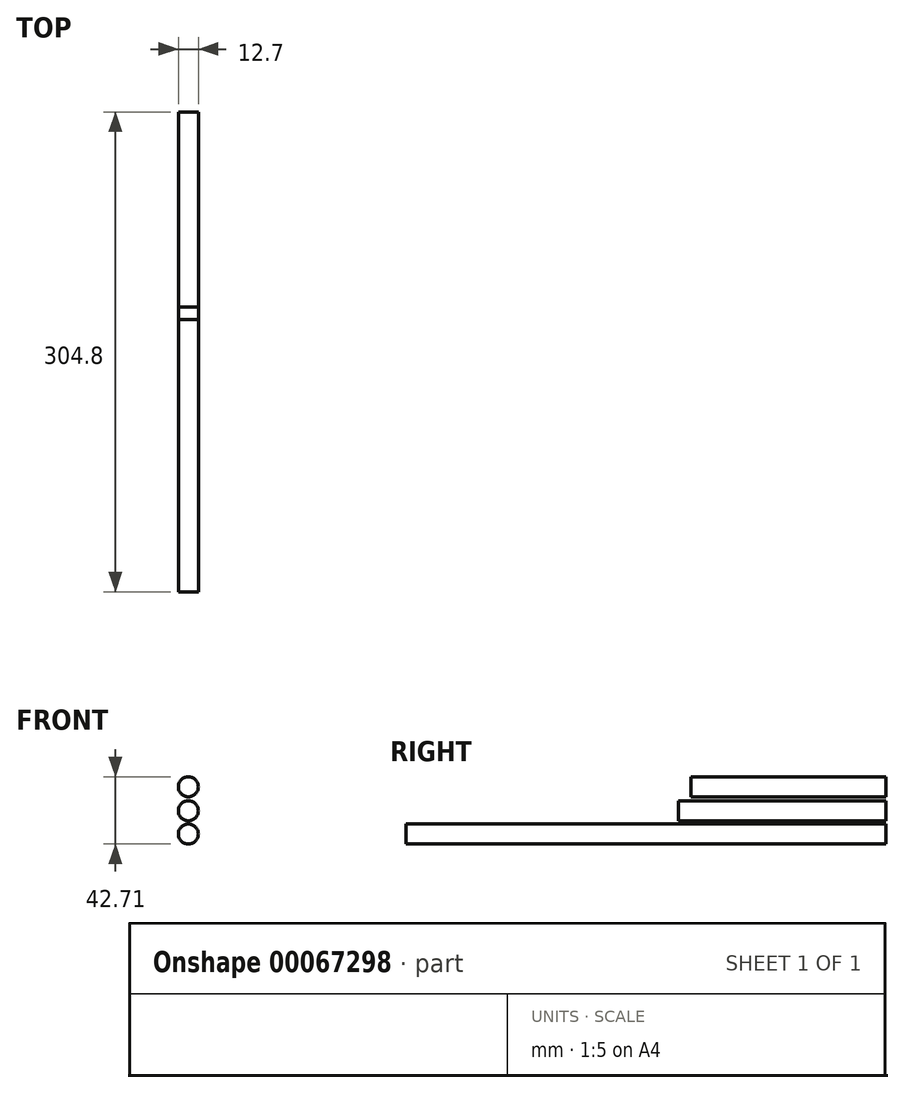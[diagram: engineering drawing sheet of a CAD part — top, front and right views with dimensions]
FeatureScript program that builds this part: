
annotation { "Feature Type Name" : "Feature", "Feature Type Description" : "" }
export const myFeature = defineFeature(function(context is Context, id is Id, definition is map)
    precondition{}
    {
        {
            var Q0;
            Q0=qCreatedBy(makeId("Front.planeOp"),FACE);
            var sketch = newSketch(context, id + "F0", { "sketchPlane" : qUnion([Q0])});
            skCircle(sketch, "E0", {"center": v(0, 0) * mm, "radius": 6.35 * mm});
            skCircle(sketch, "E1", {"center": v(0, 14.75) * mm, "radius": 6.35 * mm});
            skCircle(sketch, "E2", {"center": v(0, 30) * mm, "radius": 6.35 * mm});
            skSolve(sketch);
        }
        {
            var Q0;
            Q0=makeQuery(id+"F0.imprint","IMPRINT",FACE,{"disambiguationData":[TD([[makeQuery(id+"F0.imprint","IMPRINT",EDGE,{"derivedFrom":sQuery(id+"F0.wireOp",EDGE,"E0")}),1.0]])]});
            extrude(context, id + "F1", {"entities" : qUnion([Q0]), "depth" : 304.8 * mm});
        }
        {
            var Q0;
            Q0=makeQuery(id+"F0.imprint","IMPRINT",FACE,{"disambiguationData":[TD([[makeQuery(id+"F0.imprint","IMPRINT",EDGE,{"derivedFrom":sQuery(id+"F0.wireOp",EDGE,"E2")}),1.0]])]});
            extrude(context, id + "F2", {"entities" : qUnion([Q0]), "depth" : 123.82 * mm});
        }
        {
            var Q0;
            Q0=makeQuery(id+"F0.imprint","IMPRINT",FACE,{"disambiguationData":[TD([[makeQuery(id+"F0.imprint","IMPRINT",EDGE,{"derivedFrom":sQuery(id+"F0.wireOp",EDGE,"E1")}),1.0]])]});
            extrude(context, id + "F3", {"entities" : qUnion([Q0]), "depth" : 131.76 * mm});
        }
    });
